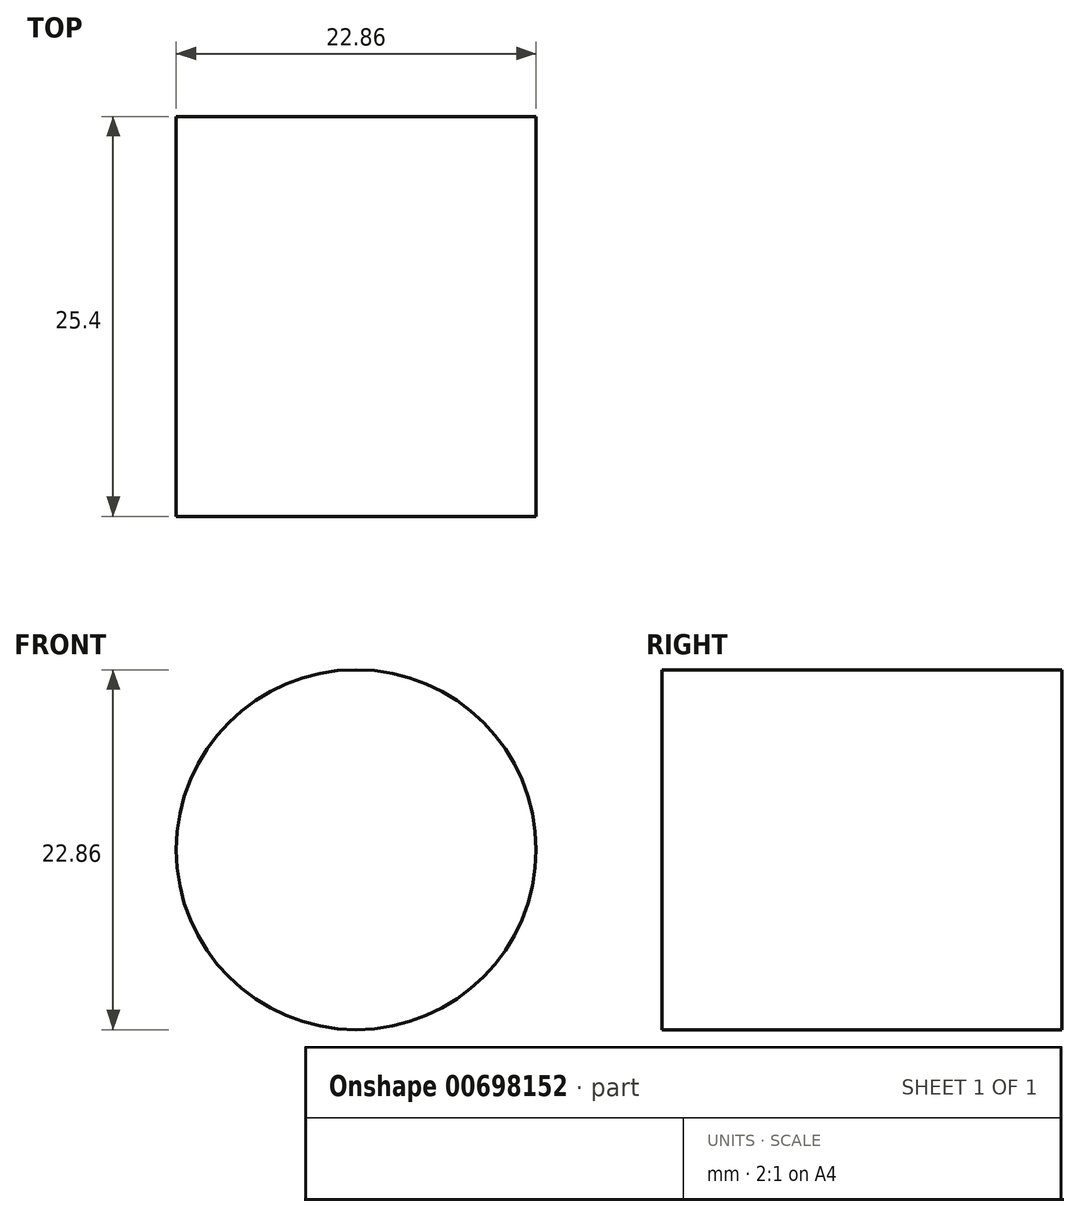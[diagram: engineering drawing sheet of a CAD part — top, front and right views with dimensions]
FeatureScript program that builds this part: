
annotation { "Feature Type Name" : "Feature", "Feature Type Description" : "" }
export const myFeature = defineFeature(function(context is Context, id is Id, definition is map)
    precondition{}
    {
        {
            var Q0;
            Q0=qCreatedBy(makeId("Front.planeOp"),FACE);
            var sketch = newSketch(context, id + "F0", { "sketchPlane" : qUnion([Q0])});
            skCircle(sketch, "E0", {"center": v(0, 0) * mm, "radius": 11.43 * mm});
            skSolve(sketch);
        }
        {
            var Q0;
            Q0=qSketchRegion(id+"F0",true);
            extrude(context, id + "F1", {"entities" : qUnion([Q0]), "depth" : 25.4 * mm, "offsetDistance" : 25.4 * mm});
        }
    });
